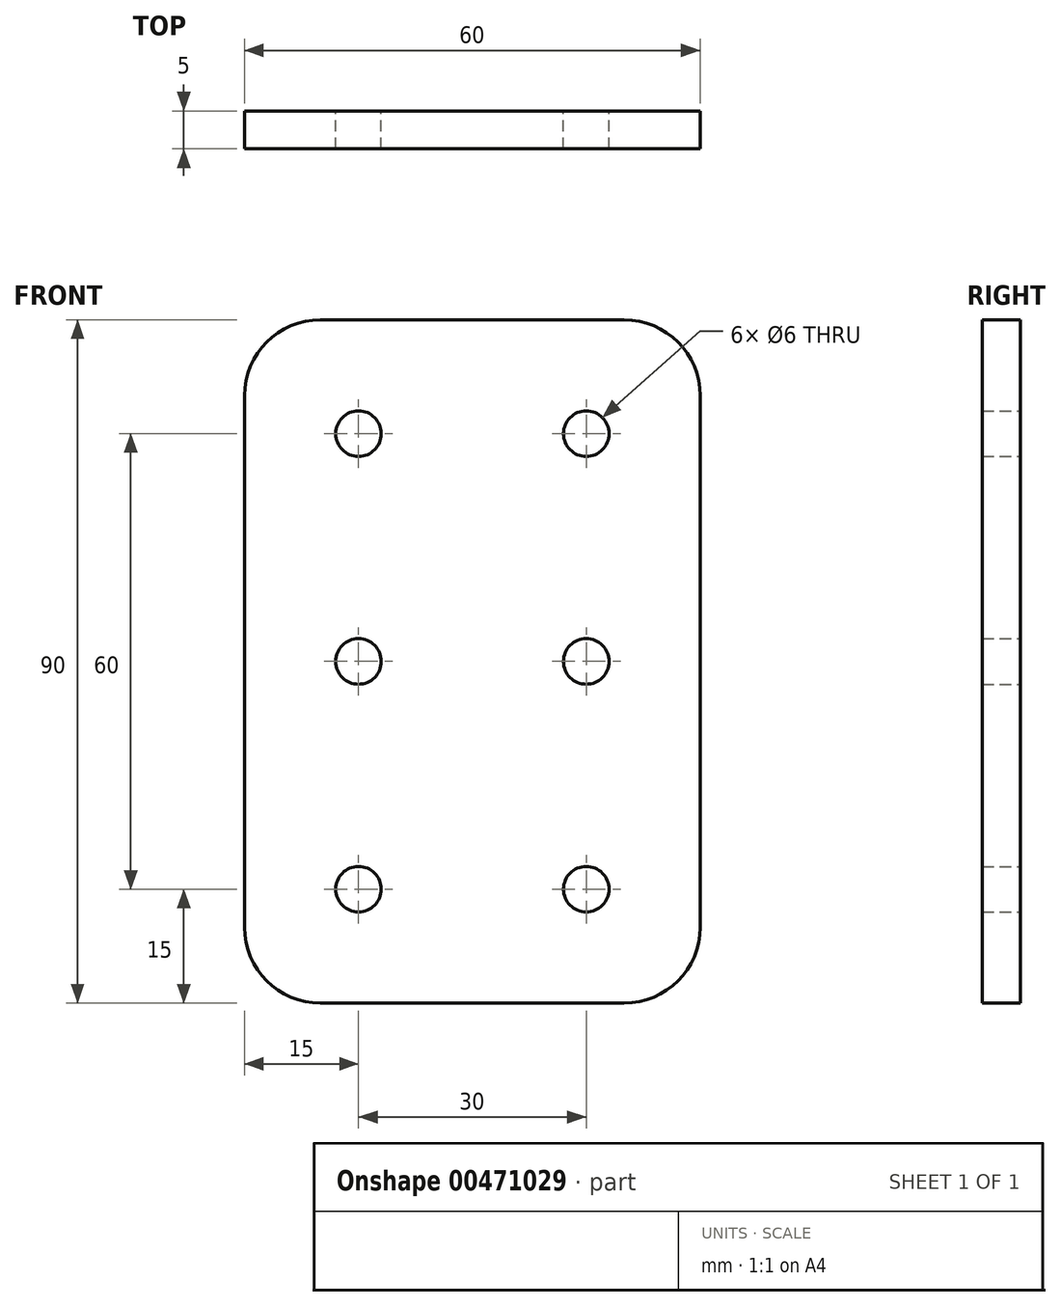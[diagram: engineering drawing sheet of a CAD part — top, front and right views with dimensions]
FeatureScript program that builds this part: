
annotation { "Feature Type Name" : "Feature", "Feature Type Description" : "" }
export const myFeature = defineFeature(function(context is Context, id is Id, definition is map)
    precondition{}
    {
        {
            var Q0;
            Q0=qCreatedBy(makeId("Front.planeOp"),FACE);
            var sketch = newSketch(context, id + "F0", { "sketchPlane" : qUnion([Q0])});
            skCircle(sketch, "E0", {"center": v(-15, 30) * mm, "radius": 3 * mm});
            skCircle(sketch, "E1", {"center": v(-15, 0) * mm, "radius": 3 * mm});
            skCircle(sketch, "E2", {"center": v(-15, -30) * mm, "radius": 3 * mm});
            skCircle(sketch, "E3", {"center": v(15, -30) * mm, "radius": 3 * mm});
            skCircle(sketch, "E4", {"center": v(15, 0) * mm, "radius": 3 * mm});
            skCircle(sketch, "E5", {"center": v(15, 30) * mm, "radius": 3 * mm});
            skLineSegment(sketch, "E6.bottom", {"start": v(-20, 45) * mm, "end": v(20, 45) * mm});
            skLineSegment(sketch, "E6.top", {"start": v(-20, -45) * mm, "end": v(20, -45) * mm});
            skLineSegment(sketch, "E6.left", {"start": v(-30, 35) * mm, "end": v(-30, -35) * mm});
            skLineSegment(sketch, "E6.right", {"start": v(30, 35) * mm, "end": v(30, -35) * mm});
            skPoint(sketch, "E7.visualSharp", {"position": v(-30, 45) * mm});
            skArc(sketch, "E7.filletArc", {"start": v(-20, 45) * mm, "mid": v(-27.07, 42.07) * mm, "end": v(-30, 35) * mm});
            skPoint(sketch, "E8.visualSharp", {"position": v(-30, -45) * mm});
            skArc(sketch, "E8.filletArc", {"start": v(-30, -35) * mm, "mid": v(-27.07, -42.07) * mm, "end": v(-20, -45) * mm});
            skPoint(sketch, "E9.visualSharp", {"position": v(30, -45) * mm});
            skArc(sketch, "E9.filletArc", {"start": v(20, -45) * mm, "mid": v(27.07, -42.07) * mm, "end": v(30, -35) * mm});
            skPoint(sketch, "E10.visualSharp", {"position": v(30, 45) * mm});
            skArc(sketch, "E10.filletArc", {"start": v(30, 35) * mm, "mid": v(27.07, 42.07) * mm, "end": v(20, 45) * mm});
            skSolve(sketch);
        }
        {
            var Q0;
            Q0 = qSketchRegion(id + "F0", true);
            extrude(context, id + "F1", {"entities" : qUnion([Q0]), "depth" : 5 * mm});
        }
    });
